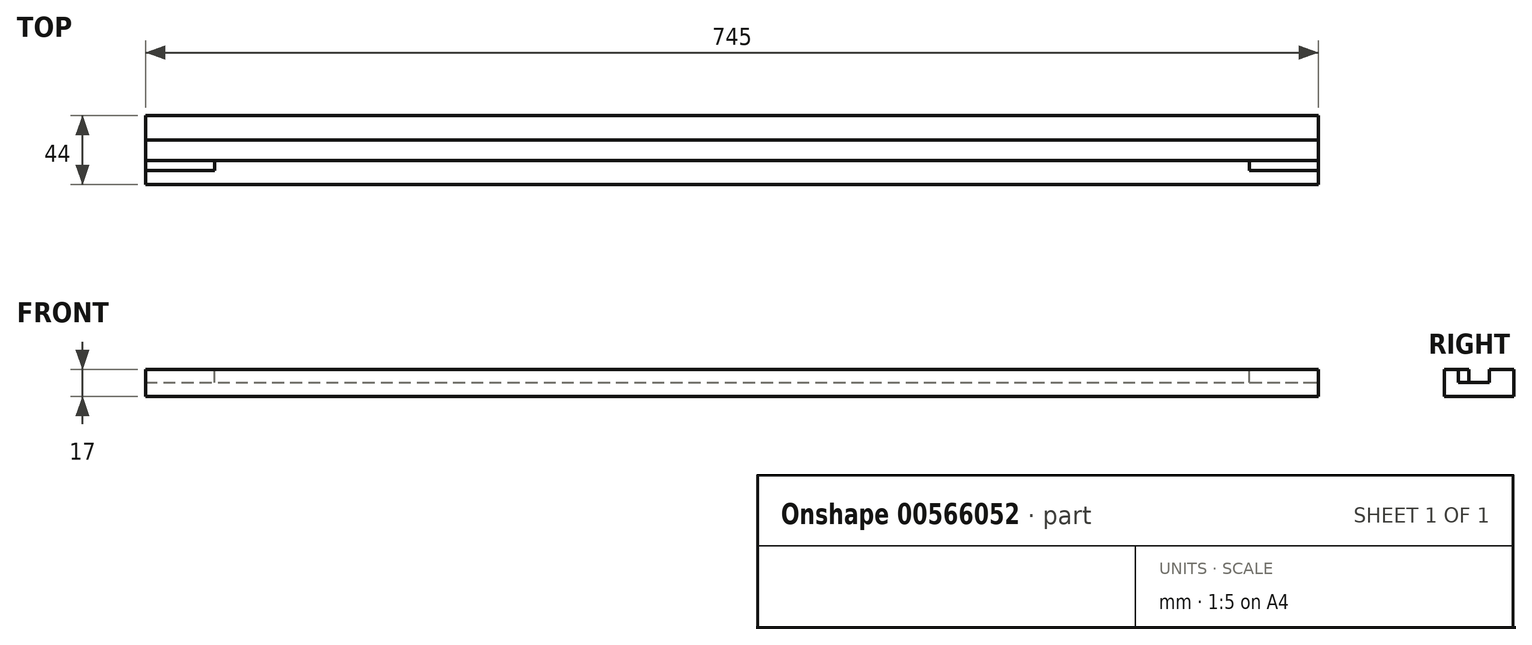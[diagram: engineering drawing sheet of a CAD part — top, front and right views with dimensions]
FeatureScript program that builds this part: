
annotation { "Feature Type Name" : "Feature", "Feature Type Description" : "" }
export const myFeature = defineFeature(function(context is Context, id is Id, definition is map)
    precondition{}
    {
        {
            var Q0;
            Q0=qCreatedBy(makeId("Top.planeOp"),FACE);
            var sketch = newSketch(context, id + "F0", { "sketchPlane" : qUnion([Q0])});
            skLineSegment(sketch, "E0.bottom", {"start": v(-207.58, 0) * mm, "end": v(537.42, 0) * mm});
            skLineSegment(sketch, "E0.top", {"start": v(-207.58, -44) * mm, "end": v(537.42, -44) * mm});
            skLineSegment(sketch, "E0.left", {"start": v(-207.58, 0) * mm, "end": v(-207.58, -44) * mm});
            skLineSegment(sketch, "E0.right", {"start": v(537.42, 0) * mm, "end": v(537.42, -44) * mm});
            skSolve(sketch);
        }
        {
            var Q0;
            Q0 = qSketchRegion(id + "F0", true);
            extrude(context, id + "F1", {"entities" : qUnion([Q0]), "depth" : 17 * mm, "offsetDistance" : 25 * mm});
        }
        {
            var Q0;
            Q0=makeQuery(id+"F1.opExtrude","SWEPT_FACE",FACE,{"disambiguationData":[OSD([sQuery(id+"F0.wireOp",EDGE,"E0.right")])]});
            var sketch = newSketch(context, id + "F2", { "sketchPlane" : qUnion([Q0])});
            skLineSegment(sketch, "E1.bottom", {"start": v(-28.5, 17) * mm, "end": v(-15.54, 17) * mm});
            skLineSegment(sketch, "E1.top", {"start": v(-28.5, 8.99) * mm, "end": v(-15.54, 8.99) * mm});
            skLineSegment(sketch, "E1.left", {"start": v(-28.5, 17) * mm, "end": v(-28.5, 8.99) * mm});
            skLineSegment(sketch, "E1.right", {"start": v(-15.54, 17) * mm, "end": v(-15.54, 8.99) * mm});
            skSolve(sketch);
        }
        {
            var Q0;
            Q0 = qSketchRegion(id + "F2", true);
            extrude(context, id + "F3", {"entities" : qUnion([Q0]), "operationType" : NewBodyOperationType.REMOVE, "oppositeDirection" : true, "depth" : 745 * mm, "offsetDistance" : 25 * mm});
        }
        {
            var Q0;
            {var subQ0=sQuery(id+"F0.wireOp",EDGE,"E0.top");var subQ1=sQuery(id+"F0.wireOp",EDGE,"E0.left");var subQ2=sQuery(id+"F0.wireOp",EDGE,"E0.right");Q0=makeQuery(id+"F3.boolean.opBoolean","SPLIT",FACE,{"disambiguationData":[TD([makeQuery(id+"F1.opExtrude","SWEPT_FACE",FACE,{"disambiguationData":[OSD([subQ0])]})])],"derivedFrom":makeQuery(id+"F1.opExtrude","CAP_FACE",FACE,{"disambiguationData":[OSD([sQuery(id+"F0.wireOp",EDGE,"E0.bottom"),subQ0,subQ1,subQ2])],"isStart":false})});}
            var sketch = newSketch(context, id + "F4", { "sketchPlane" : qUnion([Q0])});
            skLineSegment(sketch, "E2.bottom", {"start": v(537.42, -28.5) * mm, "end": v(493.42, -28.5) * mm});
            skLineSegment(sketch, "E2.top", {"start": v(537.42, -35) * mm, "end": v(493.42, -35) * mm});
            skLineSegment(sketch, "E2.left", {"start": v(537.42, -28.5) * mm, "end": v(537.42, -35) * mm});
            skLineSegment(sketch, "E2.right", {"start": v(493.42, -28.5) * mm, "end": v(493.42, -35) * mm});
            skSolve(sketch);
        }
        {
            var Q0;
            Q0 = qSketchRegion(id + "F4", true);
            extrude(context, id + "F5", {"entities" : qUnion([Q0]), "operationType" : NewBodyOperationType.REMOVE, "oppositeDirection" : true, "depth" : 8 * mm, "offsetDistance" : 25 * mm});
        }
        {
            var Q0;
            {var subQ0=sQuery(id+"F0.wireOp",EDGE,"E0.top");var subQ1=sQuery(id+"F0.wireOp",EDGE,"E0.left");var subQ2=sQuery(id+"F0.wireOp",EDGE,"E0.right");Q0=makeQuery(id+"F3.boolean.opBoolean","SPLIT",FACE,{"disambiguationData":[TD([makeQuery(id+"F1.opExtrude","SWEPT_FACE",FACE,{"disambiguationData":[OSD([subQ0])]})])],"derivedFrom":makeQuery(id+"F1.opExtrude","CAP_FACE",FACE,{"disambiguationData":[OSD([sQuery(id+"F0.wireOp",EDGE,"E0.bottom"),subQ0,subQ1,subQ2])],"isStart":false})});}
            var sketch = newSketch(context, id + "F6", { "sketchPlane" : qUnion([Q0])});
            skLineSegment(sketch, "E3.bottom", {"start": v(-207.58, -28.5) * mm, "end": v(-163.58, -28.5) * mm});
            skLineSegment(sketch, "E3.top", {"start": v(-207.58, -35) * mm, "end": v(-163.58, -35) * mm});
            skLineSegment(sketch, "E3.left", {"start": v(-207.58, -28.5) * mm, "end": v(-207.58, -35) * mm});
            skLineSegment(sketch, "E3.right", {"start": v(-163.58, -28.5) * mm, "end": v(-163.58, -35) * mm});
            skSolve(sketch);
        }
        {
            var Q0;
            Q0 = qSketchRegion(id + "F6", true);
            extrude(context, id + "F7", {"entities" : qUnion([Q0]), "operationType" : NewBodyOperationType.REMOVE, "oppositeDirection" : true, "depth" : 8 * mm, "offsetDistance" : 25 * mm});
        }
    });
